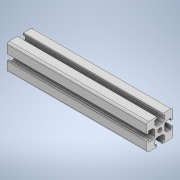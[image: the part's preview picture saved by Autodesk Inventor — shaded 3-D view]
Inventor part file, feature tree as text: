
AUTODESK INVENTOR PART (.ipt)
format: ipt  version: 2020.2 (Build 242310000, 310)  size: 176,640 bytes
history: native  units: in
note: dims shown in document units (in); Inventor stores cm internally (conversion verified against a paired STEP export)
features: extrude x1, sketch x1
ambient origin geometry x8: Origin, YZ Plane, XZ Plane, XY Plane, X Axis, Y Axis, Z Axis, Center Point
bodies: Solid1 (feature_tree)
feature tree (2):
  extrude  "Extrusion1"  Depth=0.29in
  sketch  "Sketch2"  dims[d9=0.2325in d18=0.055in d20=0.055in d34=0.29in d35=0.055in d37=0.058in d38=0.1225in d39=0.081in d40=135.0deg d41=0.17in d42=0.081in d43=0.058in d44=0.055in d45=0.75in d46=0.055in d47=1.5748in d49=360.0deg d51=0.2348in d52=0.232in d56=0.75in d58=0.125in d61=0.055in d62=0.055in d63=0.055in d64=0.055in d65=1.5748in d67=360.0deg d69=4.0in d70=0.0in d71=0.1225in]
